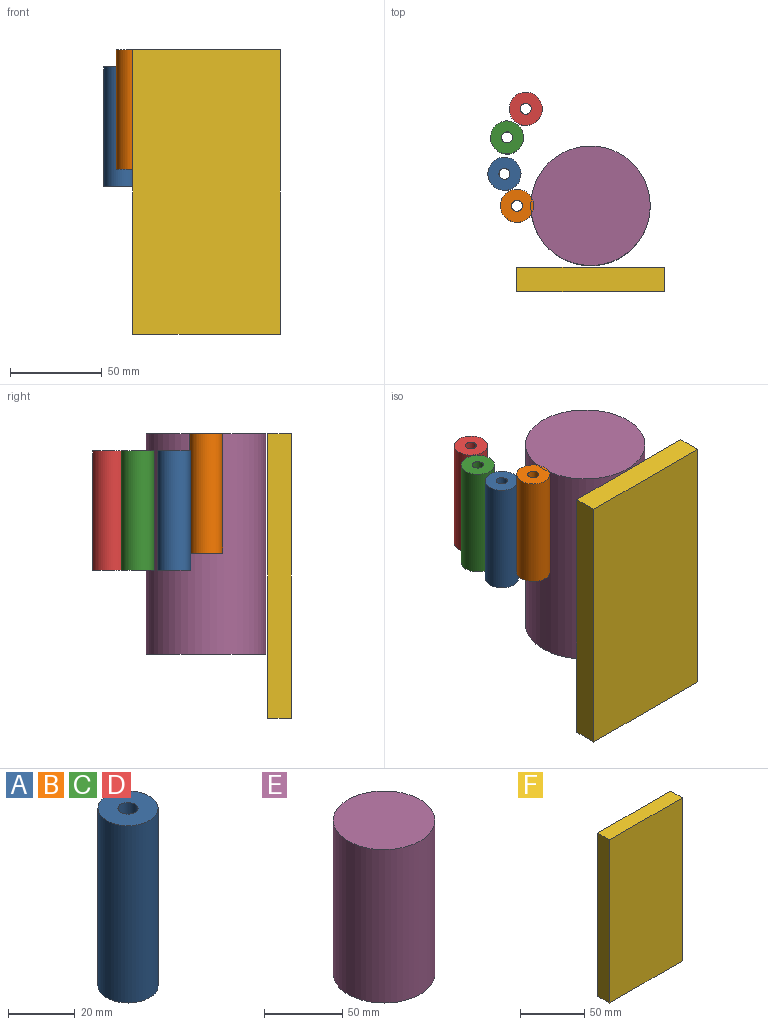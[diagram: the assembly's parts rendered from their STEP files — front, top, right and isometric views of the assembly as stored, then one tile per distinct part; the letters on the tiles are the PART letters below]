
ASSEMBLY  parts=6 mates=2
PART A: 4 faces, bbox 18x18x65 mm
  f0: cylinder r=3mm len=65mm, axis (0,0,-1), area 1225.2mm2, adj f2,f3
  f1: cylinder r=9mm len=65mm, axis (0,0,-1), area 3675.7mm2, adj f2,f3
  f2: plane 18x18mm, normal (0,0,1), area 226.2mm2, adj f0,f1
  f3: plane 18x18mm, normal (0,0,-1), area 226.2mm2, adj f0,f1
PART B: same geometry as A
PART C: same geometry as A
PART D: same geometry as A
PART E: 3 faces, bbox 65x65x120 mm
  f0: cylinder r=32.5mm len=120mm, axis (0,0,-1), area 24504.4mm2, adj f1,f2
  f1: plane 65x65mm, normal (0,0,1), area 3318.3mm2, adj f0
  f2: plane 65x65mm, normal (0,0,-1), area 3318.3mm2, adj f0
PART F: 6 faces, bbox 80x13x155 mm
  f0: plane 155x80mm, normal (0,1,0), area 12400mm2, adj f1,f3,f4,f5
  f1: plane 155x13mm, normal (-1,0,0), area 2015mm2, adj f0,f2,f4,f5
  f2: plane 155x80mm, normal (0,-1,0), area 12400mm2, adj f1,f3,f4,f5
  f3: plane 155x13mm, normal (1,0,0), area 2015mm2, adj f0,f2,f4,f5
  f4: plane 80x13mm, normal (0,0,1), area 1040mm2, adj f0,f1,f2,f3
  f5: plane 80x13mm, normal (0,0,-1), area 1040mm2, adj f0,f1,f2,f3
PLACE A rot(axis=(0,0,1),0.6deg) t=(-55.45,6.37,-14.49)mm
PLACE B rot(axis=(0,0,1),0deg) t=(-48.65,-11.02,-5)mm
PLACE C rot(axis=(0,0,1),2.2deg) t=(-54.05,26.17,-14.49)mm
PLACE D rot(axis=(0,0,1),2.2deg) t=(-43.9,41.74,-14.49)mm
PLACE E t=(-8.65,-11.02,-60)mm
PLACE F t=(-8.65,-51.02,-95)mm
MATE fastened B.f0 <-> E.f1  axis (0,0,1) through (-48.65,-11.02,60)mm
MATE slider F.f4 <-> E.f1  axis (0,0,1) through (-8.65,-51.02,60)mm
